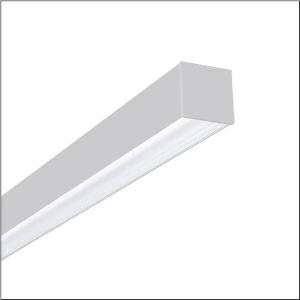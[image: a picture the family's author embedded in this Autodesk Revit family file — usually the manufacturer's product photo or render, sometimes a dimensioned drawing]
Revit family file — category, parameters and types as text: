
# Revit family: silica_r_5mx31bd2w4a_93b3
name_source: partatom
category: Lighting Fixtures
units: mm (PartAtom-declared; Revit-internal decimal feet)

## family parameters
Cut with Voids When Loaded = No
Host = Face
Light Source = No
Part Type = Normal
Room Calculation Point = No
Round Connector Dimension = Use Diameter
Shared = No

## types (1)
- --- (1 x LED, 14160 lm, 92.6 W, 4000K)
    Apparent Load = 93 VA
    CIE Flux Codes = 82 97 100 70 100
    Color Rendering = 80
    Color Temperature = 4000K
    Default Elevation = 1800 mm
    Description = Silica®, office luminaire, of aluminium, light emission: direct/indirect distribution, primary light characteristic: symmetric, installation type: suspended mounting, LED, rated luminous flux: 14.160lm, luminous efficacy: 153lm/W, light colour: 840, colour temperature: 4000K, control gear: ECG DALI, with terminal, 3+2-pole, max. 2.5mm², mains connection: 230V, AC, 50/60Hz, connection cable inclusive, cable length: 1,5m, rated input power: 93W, luminaire housing, of aluminium, traffic white (RAL 9016), length: 2.844mm, width: 65mm, height: 64mm, protection rating (complete): IP20, insulation class (complete): insulation class I (protective earthing), certification: CE, permissible operating ambient temperature: 0..+35°C, standard: EN 50419, packaging unit: 1 piece
    Height = 64 mm
    Lamp = 1 x LED
    Lamp Light Flux = 14160 lm
    Lamp Power = 92.6 W
    Lamp count = 1
    Length = 2845 mm
    Luminous efficacy = 153 lm/W
    Manufacturer = Siteco
    ModVariant = No
    Model = 5MX31BD2W4A
    Mounting Place = Ceiling
    Mounting Type = Pendant
    Number of Poles = 1
    OnlyDefault = Yes
    Power Factor = 1
    Product Name = Silica®
    Product group = office luminaire | ceiling pendant
    ProductGroupID = 902
    Protection Class = Protection class I
    Protection Degree = IP 20
    RLX_Detail_Level = 1
    RLX_Emergency_Light_Flux = 0 lm
    RLX_Emergency_Type = 0
    RLX_Emergency_Type_DB = No
    RlxData = <blob elided: 28861 chars, md5=1bc58e01>
    Socket = socket
    Standby Power = 0 W
    System Light Flux = 14160 lm
    System Power = 93 W
    Type Comments = factory setting: direct and indirect light
    Type Image = l_1003924.jpg
    URL = http://relux.com
    VarID = @adj_172712
    Voltage = 0 V
    Weight = 0.00 kg
    Width = 66 mm

## geometry (parser evidence)
native form markers: Blend x4, Sweep x13
no freeform markers — native parametric forms only
